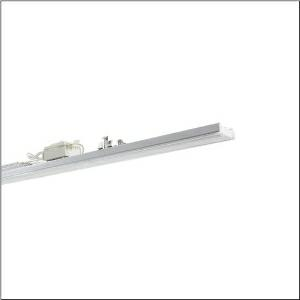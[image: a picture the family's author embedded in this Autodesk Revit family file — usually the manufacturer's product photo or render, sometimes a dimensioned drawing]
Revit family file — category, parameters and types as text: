
# Revit family: licross_11_recessed_ho_51tl1wdn4exm
name_source: partatom
category: Lighting Fixtures
units: mm (PartAtom-declared; Revit-internal decimal feet)

## family parameters
Cut with Voids When Loaded = No
Host = Face
Light Source = No
Part Type = Normal
Room Calculation Point = No
Round Connector Dimension = Use Diameter
Shared = No

## types (1)
- --- (1 x LED, 14170 lm, 76.8 W, 4000K)
    Apparent Load = 77 VA
    CIE Flux Codes = 73 94 99 100 100
    Color Rendering = 80
    Color Temperature = 4000K
    Default Elevation = 1800 mm
    Description = Licross 11 Recessed HO, luminaire insert, of sheet steel, coil coated, white, length: 1.500mm, width: 66mm, height: 67mm, LED rated luminous flux: 14.170lm, light colour: 840, SDCM (Standard Deviation of Colour Matching)MacAdam ≤ 2 SDCM (initial), control gear: DALI 2, with plug, 5-pole, with phase selection, mains connection: 220..240V, AC, 50/60Hz, rated input power: 77W, internal wiring halogen-free, primary optical cover: cover, of PMMA, light emission: direct distribution, primary light characteristic: symmetric, protection rating (complete): IP40, insulation class (complete): insulation class I (protective earthing), certification: CE, ENEC, VDE, UKCA, protection symbol: D if used in an environment without relevant dust loads with corresponding accessories, impact resistance: IK06, permissible ambient temperature for indoor applications: -25..+30°C, corresponds to IFS (International Featured Standards) requirements for safety and quality in the food industry, reducing of maximum allowable ambient temperature of 5°C with ceiling mounting, LABS conformity tested according to VDMA 24364:2018-05, The light source and the operating device comply with the requirements of the Ecodesign Regulation (EU) 2019/2020 and are replaceable in accordance with this regulation, packaging unit: 1 piece
    Height = 58 mm
    Lamp = 1 x LED
    Lamp Light Flux = 14170 lm
    Lamp Power = 76.8 W
    Lamp count = 1
    Length = 1500 mm
    Luminous efficacy = 185 lm/W
    Manufacturer = Siteco
    ModVariant = No
    Model = 51TL1WDN4EXM
    Mounting Place = Ceiling
    Mounting Type = Pendant
    Number of Poles = 1
    OnlyDefault = Yes
    Power Factor = 1
    Product Name = Licross 11 Recessed HO
    Product group = luminaire insert | ceiling pendant
    ProductGroupID = 901
    Protection Class = Protection class I
    Protection Degree = IP 40
    RLX_Detail_Level = 1
    RLX_Emergency_Light_Flux = 0 lm
    RLX_Emergency_Type = 0
    RLX_Emergency_Type_DB = No
    RlxData = <blob elided: 24901 chars, md5=e28a3edc>
    Socket = socket
    Standby Power = 0 W
    System Light Flux = 14170 lm
    System Power = 77 W
    Type Comments = factory setting: luminous flux: 100 % | dim-lin: 254 | 522 mA
    Type Image = l_1296930.jpg
    URL = http://relux.com
    VarID = @adj_066469
    Voltage = 0 V
    Weight = 0.00 kg
    Width = 66 mm

## geometry (parser evidence)
native form markers: Blend x4, Sweep x11
no freeform markers — native parametric forms only
